# Revit family: QF_BOURGEAT_chariot_cafeteria_dos_a_dos_plateaux_GN1_1_couleur
name_source: partatom
category: Equipement spécialisé
revit_build: Autodesk Revit 2015 (Build: 20140606_1530(x64)
units: mm (PartAtom-declared; Revit-internal decimal feet)

## types (4) — shared parameters
Charge max = 60.00 kg
Fabricant = BOURGEAT
Hauteur hors tout = 1700 mm  [stored 5.57743 ft]
Longueur hors tout = 670 mm  [stored 2.19816 ft]
Profondeur hors tout = 840 mm  [stored 2.75591 ft]
Spécification du Fabricant = CHARIOT CAFETERIA
URL catalogue = http://www.bourgeat.fr

## per-type parameters (varying)
| type | Modèle | Poids net à vide | panneaux_lateraux_bleus | panneaux_lateraux_rouges | panneaux_lateraux_verts |
| chariot_modele_haut_glissieres_beiges_sans_panneaux | 786006 | 22.50 kg | Non | Non | Non |
| chariot_modele_haut_glissieres_beiges_avec_2panneaux_bleus | 786306 | 28.00 kg | Oui | Non | Non |
| chariot_modele_haut_glissieres_beiges_avec_2panneaux_verts | 786406 | 28.00 kg | Non | Non | Oui |
| chariot_modele_haut_glissieres_beiges_avec_2panneaux_rouges | 786506 | 28.00 kg | Non | Oui | Non |

note: [stored X ft] marks values corroborated as IEEE doubles in the binary element streams (Revit-internal decimal feet)
